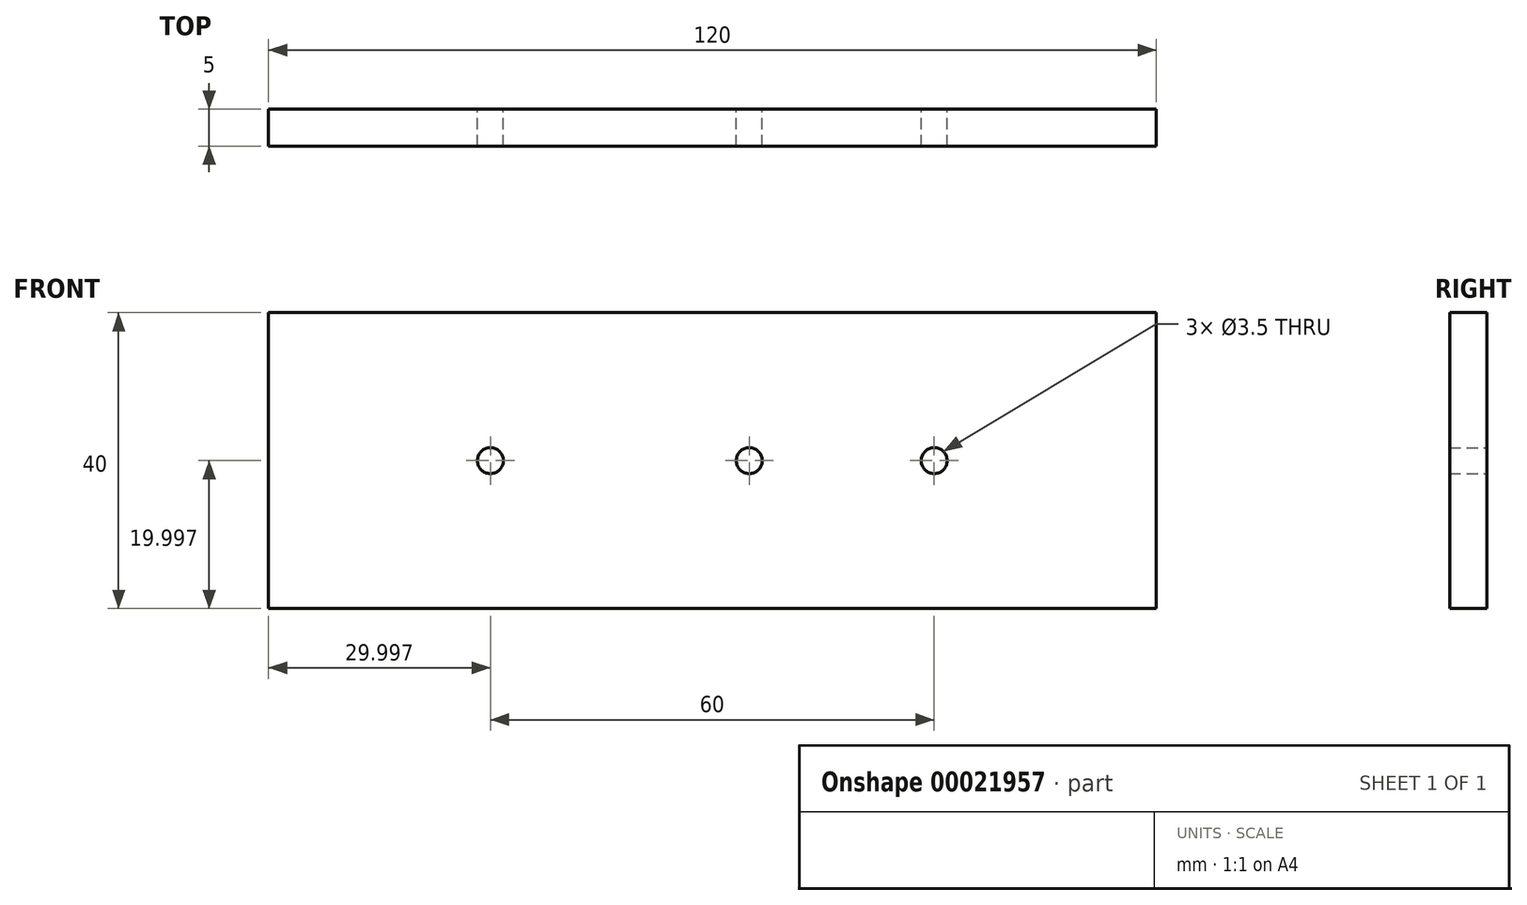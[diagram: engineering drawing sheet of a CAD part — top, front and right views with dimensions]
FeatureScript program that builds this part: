
annotation { "Feature Type Name" : "Feature", "Feature Type Description" : "" }
export const myFeature = defineFeature(function(context is Context, id is Id, definition is map)
    precondition{}
    {
        {
            var Q0;
            Q0=qCreatedBy(makeId("Front.planeOp"),FACE);
            var sketch = newSketch(context, id + "F0", { "sketchPlane" : qUnion([Q0])});
            skLineSegment(sketch, "E0.bottom", {"start": v(-32.72, 13.27) * mm, "end": v(-2.72, 13.27) * mm});
            skLineSegment(sketch, "E0.top", {"start": v(-32.72, -26.73) * mm, "end": v(57.28, -26.73) * mm});
            skLineSegment(sketch, "E0.left", {"start": v(-32.72, 13.27) * mm, "end": v(-32.72, -26.73) * mm});
            skLineSegment(sketch, "E0.right", {"start": v(57.28, -4.98) * mm, "end": v(57.28, -8.48) * mm});
            skLineSegment(sketch, "E1", {"start": v(-2.72, -6.73) * mm, "end": v(-4.47, -6.73) * mm});
            skLineSegment(sketch, "E2", {"start": v(-2.72, -6.73) * mm, "end": v(-2.72, -8.48) * mm});
            skPoint(sketch, "E3.orphan", {"position": v(57.28, -6.73) * mm});
            skLineSegment(sketch, "E4", {"start": v(57.28, 13.27) * mm, "end": v(32.28, 13.27) * mm});
            skLineSegment(sketch, "E5", {"start": v(-2.72, 13.27) * mm, "end": v(32.28, 13.27) * mm});
            skLineSegment(sketch, "E6", {"start": v(32.28, -4.98) * mm, "end": v(32.28, -8.48) * mm});
            skLineSegment(sketch, "E7", {"start": v(32.28, -6.73) * mm, "end": v(34.03, -6.73) * mm});
            skCircle(sketch, "E8", {"center": v(-2.72, -6.73) * mm, "radius": 1.75 * mm});
            skCircle(sketch, "E9", {"center": v(32.28, -6.73) * mm, "radius": 1.75 * mm});
            skCircle(sketch, "E10", {"center": v(57.28, -6.73) * mm, "radius": 1.75 * mm});
            skLineSegment(sketch, "E11", {"start": v(57.28, 13.27) * mm, "end": v(87.28, 13.27) * mm});
            skLineSegment(sketch, "E12", {"start": v(87.28, 13.27) * mm, "end": v(87.28, -26.73) * mm});
            skLineSegment(sketch, "E13", {"start": v(87.28, -26.73) * mm, "end": v(57.28, -26.73) * mm});
            skLineSegment(sketch, "E14", {"start": v(57.28, -6.73) * mm, "end": v(59.03, -6.73) * mm});
            skPoint(sketch, "E15.orphan", {"position": v(-32.72, -6.73) * mm});
            skLineSegment(sketch, "E16.trimOffspring", {"start": v(30.53, -6.73) * mm, "end": v(32.28, -6.73) * mm});
            skLineSegment(sketch, "E17.trimOffspring", {"start": v(55.53, -6.73) * mm, "end": v(57.28, -6.73) * mm});
            skPoint(sketch, "E18.orphan", {"position": v(32.28, -26.73) * mm});
            skPoint(sketch, "E19.orphan", {"position": v(87.28, -6.73) * mm});
            skSolve(sketch);
        }
        {
            var Q0;
            Q0=makeQuery(id+"F0.imprint","IMPRINT",FACE,{"disambiguationData":[TD([[makeQuery(id+"F0.imprint","IMPRINT",EDGE,{"derivedFrom":sQuery(id+"F0.wireOp",EDGE,"E0.bottom")}),-1.0]])]});
            extrude(context, id + "F1", {"entities" : qUnion([Q0]), "depth" : 5 * mm});
        }
    });
